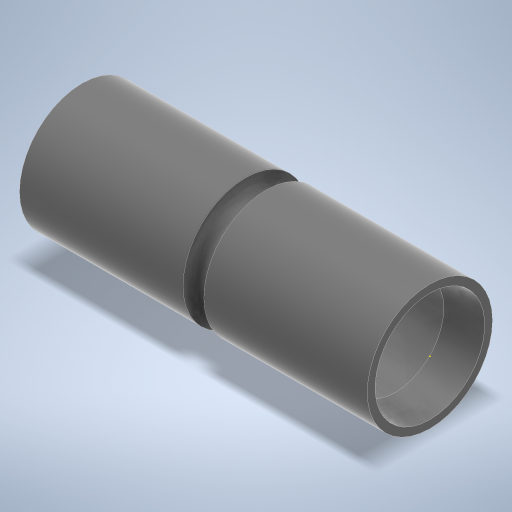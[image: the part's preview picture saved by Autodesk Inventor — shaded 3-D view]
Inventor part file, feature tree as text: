
AUTODESK INVENTOR PART (.ipt)
format: ipt  version: 2023 (Build 270158000, 158)  size: 270,848 bytes
history: native  units: mm
features: other x2, sketch x2
ambient origin geometry x8: Origin, YZ Plane, XZ Plane, XY Plane, X Axis, Y Axis, Z Axis, Center Point
bodies: Body1 (feature_tree)
feature tree (4):
  other  "Sólido1"
  sketch  "Esboço1"  dims[d4=50.0mm]
  other  "Revolução1"
  sketch  "Esboço2"  dims[d6=3.0mm d11=1.745329mm d14=5.0mm d17=1.745329mm d18=90.0deg d19=5.0mm d20=14.0mm d21=18.0mm]
